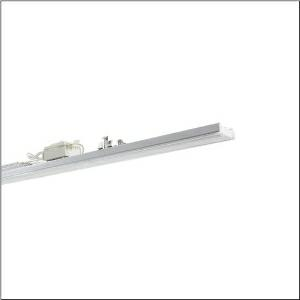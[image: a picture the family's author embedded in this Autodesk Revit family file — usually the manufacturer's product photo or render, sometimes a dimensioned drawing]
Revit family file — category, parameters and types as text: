
# Revit family: licross_r__21_recessed_ho_52tl12dn6e5m_e856
name_source: partatom
category: Lighting Fixtures
units: mm (PartAtom-declared; Revit-internal decimal feet)

## family parameters
Cut with Voids When Loaded = No
Host = Face
Light Source = No
Part Type = Normal
Room Calculation Point = No
Round Connector Dimension = Use Diameter
Shared = No

## types (1)
- --- (1 x LED, 14610 lm, 84.6 W, 6500K)
    Apparent Load = 85 VA
    CIE Flux Codes = 69 91 98 100 100
    Color Rendering = 80
    Color Temperature = 6500K
    Default Elevation = 1800 mm
    Description = Licross® 21 Recessed HO, luminaire insert, of sheet steel, galvanised, coil coated, white, length: 1.500mm, width: 66mm, height: 67mm, LED rated luminous flux: 14.610lm, light colour: 865, control gear: DALI 2, with plug, 5-pole, with phase selection, mains connection: 220..240V, AC, 50/60Hz, rated input power: 85W, internal wiring halogen-free, primary optical cover: cover, of PMMA, light emission: direct distribution, primary light characteristic: symmetric, protection rating (complete): IP40, insulation class (complete): insulation class I (protective earthing), certification: CE, ENEC, VDE, UKCA, protection symbol: D if used in an environment without relevant dust loads with corresponding accessories, impact resistance: IK06, permissible ambient temperature for indoor applications: -25..+30°C, corresponds to IFS (International Featured Standards) requirements for safety and quality in the food industry, reducing of maximum allowable ambient temperature of 5°C with ceiling mounting, LABS conformity tested according to VDMA 24364:2018-05, packaging unit: 1 piece
    Height = 58 mm
    Lamp = 1 x LED
    Lamp Light Flux = 14610 lm
    Lamp Power = 84.6 W
    Lamp count = 1
    Length = 1500 mm
    Luminous efficacy = 173 lm/W
    Manufacturer = Siteco
    ModVariant = No
    Model = 52TL12DN6E5M
    Mounting Place = Ceiling
    Mounting Type = Pendant
    Number of Poles = 1
    OnlyDefault = Yes
    Power Factor = 1
    Product Name = Licross® 21 Recessed HO
    Product group = luminaire insert | ceiling pendant
    ProductGroupID = 902
    Protection Class = Protection class I
    Protection Degree = IP 40
    RLX_Detail_Level = 1
    RLX_Emergency_Light_Flux = 0 lm
    RLX_Emergency_Type = 0
    RLX_Emergency_Type_DB = No
    RlxData = <blob elided: 24789 chars, md5=54d8bda0>
    Socket = socket
    Standby Power = 0 W
    System Light Flux = 14610 lm
    System Power = 85 W
    Type Comments = factory setting: luminous flux: 100 % | dim-lin: 254 | 484 mA
    Type Image = l_1296930.jpg
    URL = http://relux.com
    VarID = @adj_110491
    Voltage = 0 V
    Weight = 0.00 kg
    Width = 66 mm

## geometry (parser evidence)
native form markers: Blend x4, Sweep x12
no freeform markers — native parametric forms only
